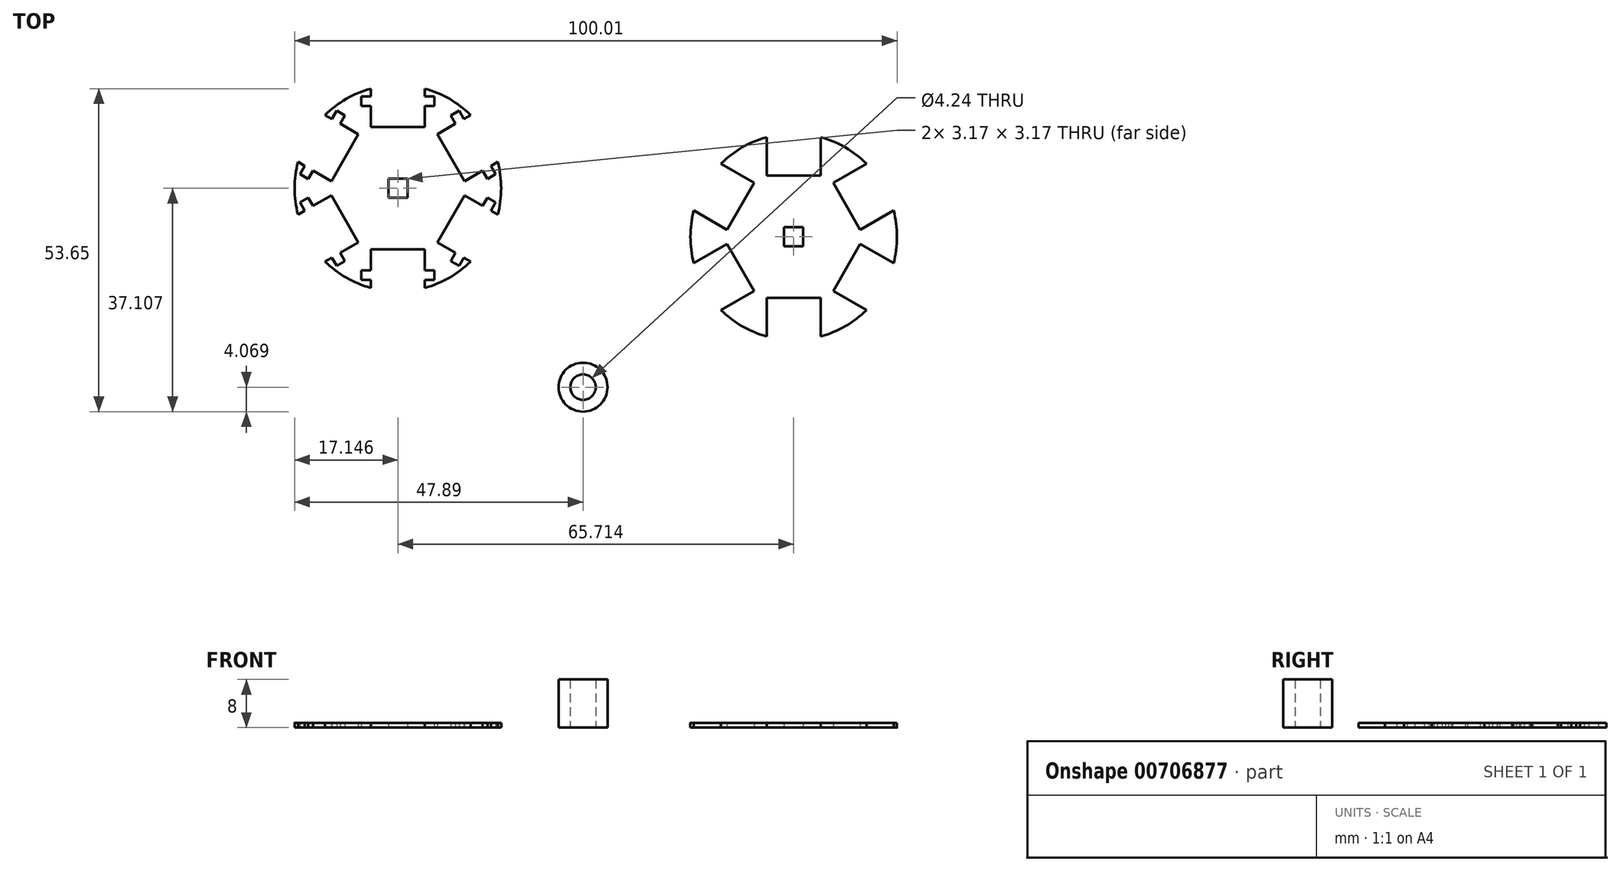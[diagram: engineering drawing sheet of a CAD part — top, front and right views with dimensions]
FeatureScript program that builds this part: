
annotation { "Feature Type Name" : "Feature", "Feature Type Description" : "" }
export const myFeature = defineFeature(function(context is Context, id is Id, definition is map)
    precondition{}
    {
        {
            var Q0;
            Q0=qCreatedBy(makeId("Top.planeOp"),FACE);
            var sketch = newSketch(context, id + "F0", { "sketchPlane" : qUnion([Q0])});
            skLineSegment(sketch, "E0.bottom", {"start": v(1.59, -1.59) * mm, "end": v(-1.59, -1.59) * mm});
            skLineSegment(sketch, "E0.top", {"start": v(1.59, 1.59) * mm, "end": v(-1.59, 1.59) * mm});
            skLineSegment(sketch, "E0.left", {"start": v(1.59, -1.59) * mm, "end": v(1.59, 1.59) * mm});
            skLineSegment(sketch, "E0.right", {"start": v(-1.59, -1.59) * mm, "end": v(-1.59, 1.59) * mm});
            skPoint(sketch, "E0.middle", {"position": v(0, 0) * mm});
            skCircle(sketch, "E1", {"center": v(0, 0) * mm, "radius": 17.15 * mm});
            skCircle(sketch, "E2", {"center": v(-34.97, -24.97) * mm, "radius": 4.06 * mm});
            skCircle(sketch, "E3", {"center": v(-34.97, -24.97) * mm, "radius": 2.12 * mm});
            skLineSegment(sketch, "E4.bottom", {"start": v(4.5, 10.16) * mm, "end": v(-4.5, 10.16) * mm});
            skLineSegment(sketch, "E4.top", {"start": v(4.5, 24.13) * mm, "end": v(-4.5, 24.13) * mm});
            skLineSegment(sketch, "E4.left", {"start": v(4.5, 10.16) * mm, "end": v(4.5, 24.13) * mm});
            skLineSegment(sketch, "E4.right", {"start": v(-4.5, 10.16) * mm, "end": v(-4.5, 24.13) * mm});
            skPoint(sketch, "E4.middle", {"position": v(0, 17.15) * mm});
            skLineSegment(sketch, "E5.1.0", {"start": v(-6.55, 8.98) * mm, "end": v(-18.65, 15.96) * mm});
            skLineSegment(sketch, "E5.1.1", {"start": v(-11.05, 1.18) * mm, "end": v(-23.15, 8.17) * mm});
            skLineSegment(sketch, "E5.1.2", {"start": v(-6.55, 8.98) * mm, "end": v(-11.05, 1.18) * mm});
            skLineSegment(sketch, "E5.2.0", {"start": v(-11.05, -1.18) * mm, "end": v(-23.15, -8.17) * mm});
            skLineSegment(sketch, "E5.2.1", {"start": v(-6.55, -8.98) * mm, "end": v(-18.65, -15.96) * mm});
            skLineSegment(sketch, "E5.2.2", {"start": v(-11.05, -1.18) * mm, "end": v(-6.55, -8.98) * mm});
            skLineSegment(sketch, "E5.3.0", {"start": v(-4.5, -10.16) * mm, "end": v(-4.5, -24.13) * mm});
            skLineSegment(sketch, "E5.3.1", {"start": v(4.5, -10.16) * mm, "end": v(4.5, -24.13) * mm});
            skLineSegment(sketch, "E5.3.2", {"start": v(-4.5, -10.16) * mm, "end": v(4.5, -10.16) * mm});
            skLineSegment(sketch, "E5.4.0", {"start": v(6.55, -8.98) * mm, "end": v(18.65, -15.96) * mm});
            skLineSegment(sketch, "E5.4.1", {"start": v(11.05, -1.18) * mm, "end": v(23.15, -8.17) * mm});
            skLineSegment(sketch, "E5.4.2", {"start": v(6.55, -8.98) * mm, "end": v(11.05, -1.18) * mm});
            skLineSegment(sketch, "E5.5.0", {"start": v(11.05, 1.18) * mm, "end": v(23.15, 8.17) * mm});
            skLineSegment(sketch, "E5.5.1", {"start": v(6.55, 8.98) * mm, "end": v(18.65, 15.96) * mm});
            skLineSegment(sketch, "E5.5.2", {"start": v(11.05, 1.18) * mm, "end": v(6.55, 8.98) * mm});
            skLineSegment(sketch, "E6.bottom", {"start": v(-4.5, 15.24) * mm, "end": v(-6.09, 15.24) * mm});
            skLineSegment(sketch, "E6.top", {"start": v(-4.5, 13.65) * mm, "end": v(-6.09, 13.65) * mm});
            skLineSegment(sketch, "E6.left", {"start": v(-4.5, 15.24) * mm, "end": v(-4.5, 13.65) * mm});
            skLineSegment(sketch, "E6.right", {"start": v(-6.09, 15.24) * mm, "end": v(-6.09, 13.65) * mm});
            skLineSegment(sketch, "E7.bottom", {"start": v(4.5, 15.24) * mm, "end": v(6.09, 15.24) * mm});
            skLineSegment(sketch, "E7.top", {"start": v(4.5, 13.65) * mm, "end": v(6.09, 13.65) * mm});
            skLineSegment(sketch, "E7.left", {"start": v(4.5, 15.24) * mm, "end": v(4.5, 13.65) * mm});
            skLineSegment(sketch, "E7.right", {"start": v(6.09, 15.24) * mm, "end": v(6.09, 13.65) * mm});
            skLineSegment(sketch, "E8.1.0", {"start": v(-10.95, 11.52) * mm, "end": v(-10.15, 12.9) * mm});
            skLineSegment(sketch, "E8.1.1", {"start": v(-9.57, 10.72) * mm, "end": v(-8.78, 12.1) * mm});
            skLineSegment(sketch, "E8.1.2", {"start": v(-10.15, 12.9) * mm, "end": v(-8.78, 12.1) * mm});
            skLineSegment(sketch, "E8.1.3", {"start": v(-15.45, 3.72) * mm, "end": v(-16.24, 2.35) * mm});
            skLineSegment(sketch, "E8.1.4", {"start": v(-16.24, 2.35) * mm, "end": v(-14.87, 1.55) * mm});
            skLineSegment(sketch, "E8.1.5", {"start": v(-14.07, 2.93) * mm, "end": v(-14.87, 1.55) * mm});
            skLineSegment(sketch, "E8.2.0", {"start": v(-15.45, -3.72) * mm, "end": v(-16.24, -2.35) * mm});
            skLineSegment(sketch, "E8.2.1", {"start": v(-14.07, -2.93) * mm, "end": v(-14.87, -1.55) * mm});
            skLineSegment(sketch, "E8.2.2", {"start": v(-16.24, -2.35) * mm, "end": v(-14.87, -1.55) * mm});
            skLineSegment(sketch, "E8.2.3", {"start": v(-10.95, -11.52) * mm, "end": v(-10.15, -12.9) * mm});
            skLineSegment(sketch, "E8.2.4", {"start": v(-10.15, -12.9) * mm, "end": v(-8.78, -12.1) * mm});
            skLineSegment(sketch, "E8.2.5", {"start": v(-9.57, -10.72) * mm, "end": v(-8.78, -12.1) * mm});
            skLineSegment(sketch, "E8.3.0", {"start": v(-4.5, -15.24) * mm, "end": v(-6.09, -15.24) * mm});
            skLineSegment(sketch, "E8.3.1", {"start": v(-4.5, -13.65) * mm, "end": v(-6.09, -13.65) * mm});
            skLineSegment(sketch, "E8.3.2", {"start": v(-6.09, -15.24) * mm, "end": v(-6.09, -13.65) * mm});
            skLineSegment(sketch, "E8.3.3", {"start": v(4.5, -15.24) * mm, "end": v(6.09, -15.24) * mm});
            skLineSegment(sketch, "E8.3.4", {"start": v(6.09, -15.24) * mm, "end": v(6.09, -13.65) * mm});
            skLineSegment(sketch, "E8.3.5", {"start": v(4.5, -13.65) * mm, "end": v(6.09, -13.65) * mm});
            skLineSegment(sketch, "E8.4.0", {"start": v(10.95, -11.52) * mm, "end": v(10.15, -12.9) * mm});
            skLineSegment(sketch, "E8.4.1", {"start": v(9.57, -10.72) * mm, "end": v(8.78, -12.1) * mm});
            skLineSegment(sketch, "E8.4.2", {"start": v(10.15, -12.9) * mm, "end": v(8.78, -12.1) * mm});
            skLineSegment(sketch, "E8.4.3", {"start": v(15.45, -3.72) * mm, "end": v(16.24, -2.35) * mm});
            skLineSegment(sketch, "E8.4.4", {"start": v(16.24, -2.35) * mm, "end": v(14.87, -1.55) * mm});
            skLineSegment(sketch, "E8.4.5", {"start": v(14.07, -2.93) * mm, "end": v(14.87, -1.55) * mm});
            skLineSegment(sketch, "E8.5.0", {"start": v(15.45, 3.72) * mm, "end": v(16.24, 2.35) * mm});
            skLineSegment(sketch, "E8.5.1", {"start": v(14.07, 2.93) * mm, "end": v(14.87, 1.55) * mm});
            skLineSegment(sketch, "E8.5.2", {"start": v(16.24, 2.35) * mm, "end": v(14.87, 1.55) * mm});
            skLineSegment(sketch, "E8.5.3", {"start": v(10.95, 11.52) * mm, "end": v(10.15, 12.9) * mm});
            skLineSegment(sketch, "E8.5.4", {"start": v(10.15, 12.9) * mm, "end": v(8.78, 12.1) * mm});
            skLineSegment(sketch, "E8.5.5", {"start": v(9.57, 10.72) * mm, "end": v(8.78, 12.1) * mm});
            skLineSegment(sketch, "E9.bottom", {"start": v(-64.13, 6.48) * mm, "end": v(-67.3, 6.48) * mm});
            skLineSegment(sketch, "E9.top", {"start": v(-64.13, 9.65) * mm, "end": v(-67.3, 9.65) * mm});
            skLineSegment(sketch, "E9.left", {"start": v(-64.13, 6.48) * mm, "end": v(-64.13, 9.65) * mm});
            skLineSegment(sketch, "E9.right", {"start": v(-67.3, 6.48) * mm, "end": v(-67.3, 9.65) * mm});
            skPoint(sketch, "E9.middle", {"position": v(-65.71, 8.07) * mm});
            skCircle(sketch, "E10", {"center": v(-65.71, 8.07) * mm, "radius": 17.15 * mm});
            skLineSegment(sketch, "E11.bottom", {"start": v(-61.21, 18.23) * mm, "end": v(-70.21, 18.23) * mm});
            skLineSegment(sketch, "E11.top", {"start": v(-61.21, 32.2) * mm, "end": v(-70.21, 32.2) * mm});
            skLineSegment(sketch, "E11.left", {"start": v(-61.21, 18.23) * mm, "end": v(-61.21, 32.2) * mm});
            skLineSegment(sketch, "E11.right", {"start": v(-70.21, 18.23) * mm, "end": v(-70.21, 32.2) * mm});
            skPoint(sketch, "E11.middle", {"position": v(-65.71, 25.21) * mm});
            skLineSegment(sketch, "E12.1.0", {"start": v(-72.26, 17.04) * mm, "end": v(-84.36, 24.03) * mm});
            skLineSegment(sketch, "E12.1.1", {"start": v(-76.76, 9.25) * mm, "end": v(-88.86, 16.24) * mm});
            skLineSegment(sketch, "E12.1.2", {"start": v(-72.26, 17.04) * mm, "end": v(-76.76, 9.25) * mm});
            skLineSegment(sketch, "E12.2.0", {"start": v(-76.76, 6.88) * mm, "end": v(-88.86, -0.1) * mm});
            skLineSegment(sketch, "E12.2.1", {"start": v(-72.26, -0.9) * mm, "end": v(-84.36, -7.9) * mm});
            skLineSegment(sketch, "E12.2.2", {"start": v(-76.76, 6.88) * mm, "end": v(-72.26, -0.9) * mm});
            skLineSegment(sketch, "E12.3.0", {"start": v(-70.21, -2.1) * mm, "end": v(-70.21, -16.06) * mm});
            skLineSegment(sketch, "E12.3.1", {"start": v(-61.21, -2.1) * mm, "end": v(-61.21, -16.06) * mm});
            skLineSegment(sketch, "E12.3.2", {"start": v(-70.21, -2.1) * mm, "end": v(-61.21, -2.1) * mm});
            skLineSegment(sketch, "E12.4.0", {"start": v(-59.16, -0.9) * mm, "end": v(-47.07, -7.9) * mm});
            skLineSegment(sketch, "E12.4.1", {"start": v(-54.66, 6.88) * mm, "end": v(-42.57, -0.1) * mm});
            skLineSegment(sketch, "E12.4.2", {"start": v(-59.16, -0.9) * mm, "end": v(-54.66, 6.88) * mm});
            skLineSegment(sketch, "E12.5.0", {"start": v(-54.66, 9.25) * mm, "end": v(-42.57, 16.24) * mm});
            skLineSegment(sketch, "E12.5.1", {"start": v(-59.16, 17.04) * mm, "end": v(-47.07, 24.03) * mm});
            skLineSegment(sketch, "E12.5.2", {"start": v(-54.66, 9.25) * mm, "end": v(-59.16, 17.04) * mm});
            skLineSegment(sketch, "E13.bottom", {"start": v(-70.21, 23.3) * mm, "end": v(-71.8, 23.3) * mm});
            skLineSegment(sketch, "E13.top", {"start": v(-70.21, 21.72) * mm, "end": v(-71.8, 21.72) * mm});
            skLineSegment(sketch, "E13.left", {"start": v(-70.21, 23.3) * mm, "end": v(-70.21, 21.72) * mm});
            skLineSegment(sketch, "E13.right", {"start": v(-71.8, 23.3) * mm, "end": v(-71.8, 21.72) * mm});
            skLineSegment(sketch, "E14.bottom", {"start": v(-61.21, 23.3) * mm, "end": v(-59.63, 23.3) * mm});
            skLineSegment(sketch, "E14.top", {"start": v(-61.21, 21.72) * mm, "end": v(-59.63, 21.72) * mm});
            skLineSegment(sketch, "E14.left", {"start": v(-61.21, 23.3) * mm, "end": v(-61.21, 21.72) * mm});
            skLineSegment(sketch, "E14.right", {"start": v(-59.63, 23.3) * mm, "end": v(-59.63, 21.72) * mm});
            skLineSegment(sketch, "E15.1.0", {"start": v(-76.66, 19.58) * mm, "end": v(-75.87, 20.96) * mm});
            skLineSegment(sketch, "E15.1.1", {"start": v(-75.29, 18.8) * mm, "end": v(-74.5, 20.17) * mm});
            skLineSegment(sketch, "E15.1.2", {"start": v(-75.87, 20.96) * mm, "end": v(-74.5, 20.17) * mm});
            skLineSegment(sketch, "E15.1.3", {"start": v(-81.16, 11.8) * mm, "end": v(-81.96, 10.42) * mm});
            skLineSegment(sketch, "E15.1.4", {"start": v(-81.96, 10.42) * mm, "end": v(-80.58, 9.62) * mm});
            skLineSegment(sketch, "E15.1.5", {"start": v(-79.79, 11) * mm, "end": v(-80.58, 9.62) * mm});
            skLineSegment(sketch, "E15.2.0", {"start": v(-81.16, 4.34) * mm, "end": v(-81.96, 5.72) * mm});
            skLineSegment(sketch, "E15.2.1", {"start": v(-79.79, 5.14) * mm, "end": v(-80.58, 6.51) * mm});
            skLineSegment(sketch, "E15.2.2", {"start": v(-81.96, 5.72) * mm, "end": v(-80.58, 6.51) * mm});
            skLineSegment(sketch, "E15.2.3", {"start": v(-76.66, -3.45) * mm, "end": v(-75.87, -4.82) * mm});
            skLineSegment(sketch, "E15.2.4", {"start": v(-75.87, -4.82) * mm, "end": v(-74.5, -4.03) * mm});
            skLineSegment(sketch, "E15.2.5", {"start": v(-75.29, -2.66) * mm, "end": v(-74.5, -4.03) * mm});
            skLineSegment(sketch, "E15.3.0", {"start": v(-70.21, -7.17) * mm, "end": v(-71.8, -7.17) * mm});
            skLineSegment(sketch, "E15.3.1", {"start": v(-70.21, -5.59) * mm, "end": v(-71.8, -5.59) * mm});
            skLineSegment(sketch, "E15.3.2", {"start": v(-71.8, -7.17) * mm, "end": v(-71.8, -5.59) * mm});
            skLineSegment(sketch, "E15.3.3", {"start": v(-61.21, -7.17) * mm, "end": v(-59.63, -7.17) * mm});
            skLineSegment(sketch, "E15.3.4", {"start": v(-59.63, -7.17) * mm, "end": v(-59.63, -5.59) * mm});
            skLineSegment(sketch, "E15.3.5", {"start": v(-61.21, -5.59) * mm, "end": v(-59.63, -5.59) * mm});
            skLineSegment(sketch, "E15.4.0", {"start": v(-54.77, -3.45) * mm, "end": v(-55.56, -4.82) * mm});
            skLineSegment(sketch, "E15.4.1", {"start": v(-56.14, -2.66) * mm, "end": v(-56.93, -4.03) * mm});
            skLineSegment(sketch, "E15.4.2", {"start": v(-55.56, -4.82) * mm, "end": v(-56.93, -4.03) * mm});
            skLineSegment(sketch, "E15.4.3", {"start": v(-50.27, 4.34) * mm, "end": v(-49.47, 5.72) * mm});
            skLineSegment(sketch, "E15.4.4", {"start": v(-49.47, 5.72) * mm, "end": v(-50.85, 6.51) * mm});
            skLineSegment(sketch, "E15.4.5", {"start": v(-51.64, 5.14) * mm, "end": v(-50.85, 6.51) * mm});
            skLineSegment(sketch, "E15.5.0", {"start": v(-50.27, 11.8) * mm, "end": v(-49.47, 10.42) * mm});
            skLineSegment(sketch, "E15.5.1", {"start": v(-51.64, 11) * mm, "end": v(-50.85, 9.62) * mm});
            skLineSegment(sketch, "E15.5.2", {"start": v(-49.47, 10.42) * mm, "end": v(-50.85, 9.62) * mm});
            skLineSegment(sketch, "E15.5.3", {"start": v(-54.77, 19.58) * mm, "end": v(-55.56, 20.96) * mm});
            skLineSegment(sketch, "E15.5.4", {"start": v(-55.56, 20.96) * mm, "end": v(-56.93, 20.17) * mm});
            skLineSegment(sketch, "E15.5.5", {"start": v(-56.14, 18.8) * mm, "end": v(-56.93, 20.17) * mm});
            skSolve(sketch);
        }
        {
            var Q0;
            Q0=makeQuery(id+"F0.imprint","IMPRINT",FACE,{"disambiguationData":[TD([[makeQuery(id+"F0.imprint","IMPRINT",EDGE,{"derivedFrom":sQuery(id+"F0.wireOp",EDGE,"E2")}),1.0]])]});
            extrude(context, id + "F1", {"entities" : qUnion([Q0]), "depth" : 8 * mm, "offsetDistance" : 25.4 * mm});
        }
        {
            var Q0;
            {var subQ0=sQuery(id+"F0.wireOp",EDGE,"E8.2.0");Q0=makeQuery(id+"F0.imprint","IMPRINT",FACE,{"disambiguationData":[TD([[makeQuery(id+"F0.imprint","IMPRINT",EDGE,{"derivedFrom":subQ0}),-1.0]])]});}
            var Q1;
            {var subQ0=sQuery(id+"F0.wireOp",EDGE,"E8.3.0");Q1=makeQuery(id+"F0.imprint","IMPRINT",FACE,{"disambiguationData":[TD([[makeQuery(id+"F0.imprint","IMPRINT",EDGE,{"derivedFrom":subQ0}),-1.0]])]});}
            var Q2;
            {var subQ0=sQuery(id+"F0.wireOp",EDGE,"E8.3.3");Q2=makeQuery(id+"F0.imprint","IMPRINT",FACE,{"disambiguationData":[TD([[makeQuery(id+"F0.imprint","IMPRINT",EDGE,{"derivedFrom":subQ0}),1.0]])]});}
            var Q3;
            {var subQ0=sQuery(id+"F0.wireOp",EDGE,"E8.4.0");Q3=makeQuery(id+"F0.imprint","IMPRINT",FACE,{"disambiguationData":[TD([[makeQuery(id+"F0.imprint","IMPRINT",EDGE,{"derivedFrom":subQ0}),-1.0]])]});}
            var Q4;
            {var subQ0=sQuery(id+"F0.wireOp",EDGE,"E8.4.3");Q4=makeQuery(id+"F0.imprint","IMPRINT",FACE,{"disambiguationData":[TD([[makeQuery(id+"F0.imprint","IMPRINT",EDGE,{"derivedFrom":subQ0}),1.0]])]});}
            var Q5;
            {var subQ0=sQuery(id+"F0.wireOp",EDGE,"E8.5.0");Q5=makeQuery(id+"F0.imprint","IMPRINT",FACE,{"disambiguationData":[TD([[makeQuery(id+"F0.imprint","IMPRINT",EDGE,{"derivedFrom":subQ0}),-1.0]])]});}
            var Q6;
            {var subQ0=sQuery(id+"F0.wireOp",EDGE,"E8.1.0");Q6=makeQuery(id+"F0.imprint","IMPRINT",FACE,{"disambiguationData":[TD([[makeQuery(id+"F0.imprint","IMPRINT",EDGE,{"derivedFrom":subQ0}),-1.0]])]});}
            var Q7;
            Q7=makeQuery(id+"F0.imprint","IMPRINT",FACE,{"disambiguationData":[TD([[makeQuery(id+"F0.imprint","IMPRINT",EDGE,{"derivedFrom":sQuery(id+"F0.wireOp",EDGE,"E0.bottom")}),1.0]])]});
            var Q8;
            Q8=makeQuery(id+"F0.imprint","IMPRINT",FACE,{"disambiguationData":[TD([[makeQuery(id+"F0.imprint","IMPRINT",EDGE,{"derivedFrom":sQuery(id+"F0.wireOp",EDGE,"E6.bottom")}),1.0]])]});
            var Q9;
            Q9=makeQuery(id+"F0.imprint","IMPRINT",FACE,{"disambiguationData":[TD([[makeQuery(id+"F0.imprint","IMPRINT",EDGE,{"derivedFrom":sQuery(id+"F0.wireOp",EDGE,"E7.bottom")}),-1.0]])]});
            var Q10;
            {var subQ0=sQuery(id+"F0.wireOp",EDGE,"E8.5.3");Q10=makeQuery(id+"F0.imprint","IMPRINT",FACE,{"disambiguationData":[TD([[makeQuery(id+"F0.imprint","IMPRINT",EDGE,{"derivedFrom":subQ0}),1.0]])]});}
            var Q11;
            {var subQ0=sQuery(id+"F0.wireOp",EDGE,"E8.1.3");Q11=makeQuery(id+"F0.imprint","IMPRINT",FACE,{"disambiguationData":[TD([[makeQuery(id+"F0.imprint","IMPRINT",EDGE,{"derivedFrom":subQ0}),1.0]])]});}
            var Q12;
            {var subQ0=sQuery(id+"F0.wireOp",EDGE,"E8.2.3");Q12=makeQuery(id+"F0.imprint","IMPRINT",FACE,{"disambiguationData":[TD([[makeQuery(id+"F0.imprint","IMPRINT",EDGE,{"derivedFrom":subQ0}),1.0]])]});}
            extrude(context, id + "F2", {"entities" : qUnion([Q0, Q1, Q2, Q3, Q4, Q5, Q6, Q7, Q8, Q9, Q10, Q11, Q12]), "depth" : 0.8 * mm, "offsetDistance" : 25.4 * mm});
        }
        {
            var Q0;
            Q0=makeQuery(id+"F0.imprint","IMPRINT",FACE,{"disambiguationData":[TD([[makeQuery(id+"F0.imprint","IMPRINT",EDGE,{"derivedFrom":sQuery(id+"F0.wireOp",EDGE,"E9.bottom")}),1.0]])]});
            extrude(context, id + "F3", {"entities" : qUnion([Q0]), "depth" : 0.8 * mm, "offsetDistance" : 25.4 * mm});
        }
    });
